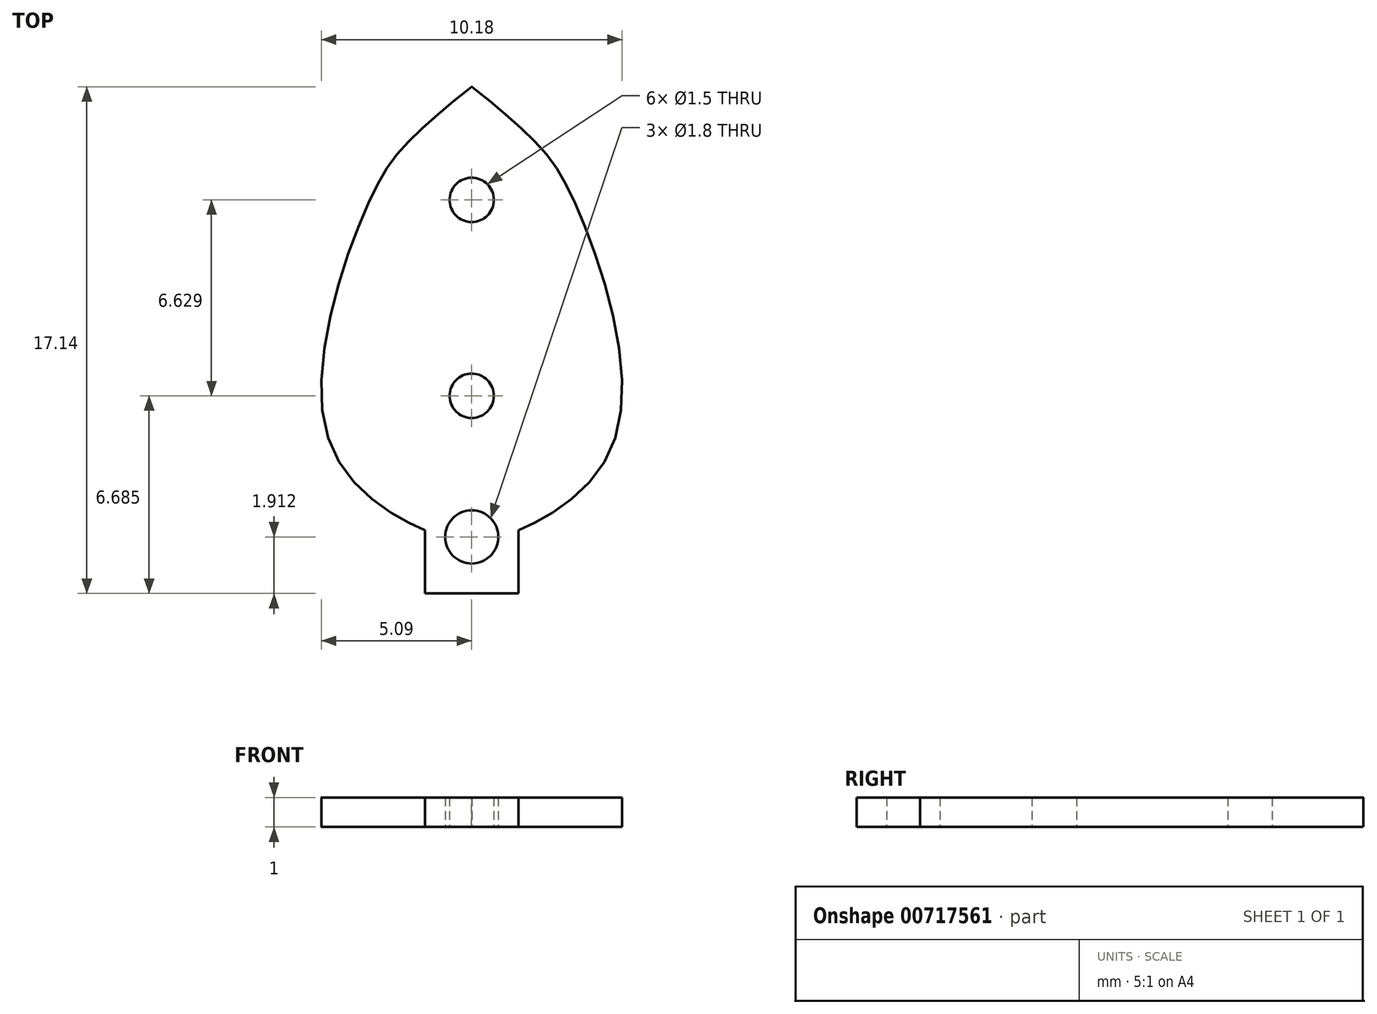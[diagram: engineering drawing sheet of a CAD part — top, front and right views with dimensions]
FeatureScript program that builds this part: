
annotation { "Feature Type Name" : "Feature", "Feature Type Description" : "" }
export const myFeature = defineFeature(function(context is Context, id is Id, definition is map)
    precondition{}
    {
        {
            var Q0;
            Q0=qCreatedBy(makeId("Top.planeOp"),FACE);
            var sketch = newSketch(context, id + "F0", { "sketchPlane" : qUnion([Q0])});
            skCircle(sketch, "E0", {"center": v(0, -12.28) * mm, "radius": 0.9 * mm});
            skLineSegment(sketch, "E1", {"start": v(0, -14.19) * mm, "end": v(1.58, -14.19) * mm});
            skLineSegment(sketch, "E2", {"start": v(1.58, -14.19) * mm, "end": v(1.58, -12.05) * mm});
            skFitSpline(sketch, "E3", {"points": [v(1.58, -12.05) * mm, v(4.84, -9) * mm, v(3.55, -1.1) * mm, v(1.8, 1.44) * mm, v(0, 2.95) * mm, v(0, 2.94) * mm], "startDerivative": vector(11.45, 4.64) * mm, "endDerivative": vector(0.98, -3.6) * mm});
            skFitSpline(sketch, "E4.MirrorCS", {"points": [v(-1.58, -12.05) * mm, v(-4.84, -9) * mm, v(-3.55, -1.1) * mm, v(-1.8, 1.44) * mm, v(0, 2.95) * mm, v(0, 2.94) * mm], "startDerivative": vector(-11.45, 4.64) * mm, "endDerivative": vector(-0.98, -3.6) * mm});
            skLineSegment(sketch, "E5.MirrorCS", {"start": v(-1.58, -14.19) * mm, "end": v(-1.58, -12.05) * mm});
            skLineSegment(sketch, "E6.MirrorCS", {"start": v(0, -14.19) * mm, "end": v(-1.58, -14.19) * mm});
            skCircle(sketch, "E7", {"center": v(0, -0.88) * mm, "radius": 0.75 * mm});
            skCircle(sketch, "E8", {"center": v(0, -7.5) * mm, "radius": 0.75 * mm});
            skSolve(sketch);
        }
        {
            var Q0;
            Q0 = qSketchRegion(id + "F0", true);
            extrude(context, id + "F1", {"entities" : qUnion([Q0]), "depth" : 1 * mm, "offsetDistance" : 25.4 * mm});
        }
    });
